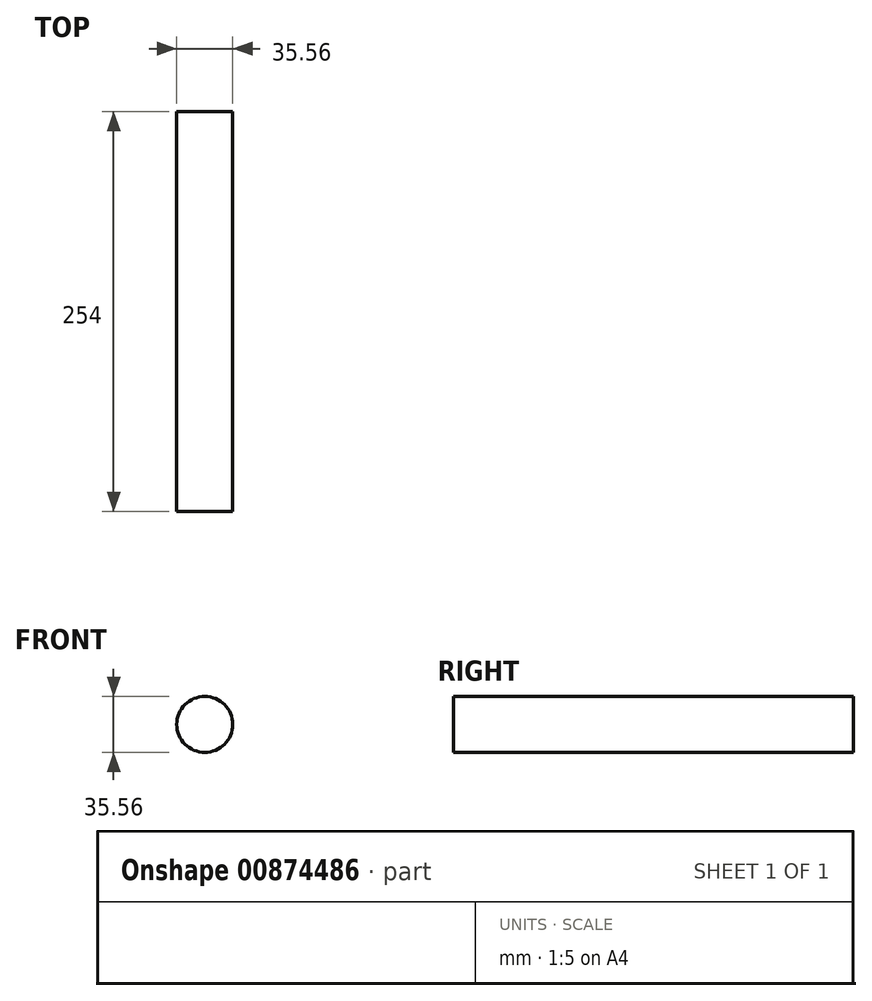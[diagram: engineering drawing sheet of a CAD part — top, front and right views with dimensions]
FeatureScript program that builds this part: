
annotation { "Feature Type Name" : "Feature", "Feature Type Description" : "" }
export const myFeature = defineFeature(function(context is Context, id is Id, definition is map)
    precondition{}
    {
        {
            var Q0;
            Q0=qCreatedBy(makeId("Front.planeOp"),FACE);
            var sketch = newSketch(context, id + "F0", { "sketchPlane" : qUnion([Q0])});
            skCircle(sketch, "E0", {"center": v(0, 0) * mm, "radius": 17.78 * mm});
            skSolve(sketch);
        }
        {
            var Q0;
            Q0=makeQuery(id+"F0.imprint","IMPRINT",FACE,{"disambiguationData":[TD([[makeQuery(id+"F0.imprint","IMPRINT",EDGE,{"derivedFrom":sQuery(id+"F0.wireOp",EDGE,"E0")}),1.0]])]});
            extrude(context, id + "F1", {"entities" : qUnion([Q0]), "oppositeDirection" : true, "depth" : 254 * mm, "offsetDistance" : 25.4 * mm});
        }
    });
